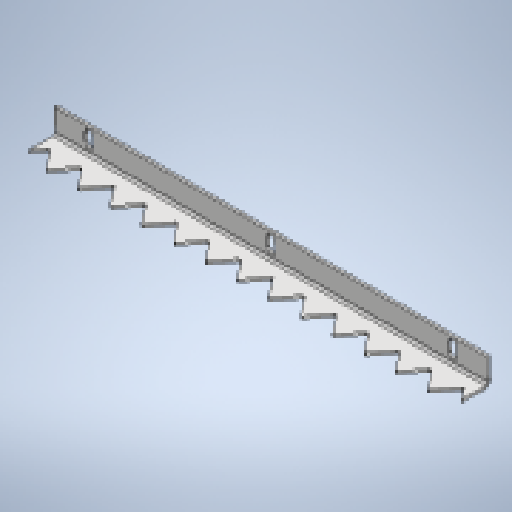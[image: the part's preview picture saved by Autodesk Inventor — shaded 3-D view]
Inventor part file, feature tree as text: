
AUTODESK INVENTOR PART (.ipt)
format: ipt  version: 2025.1 (Build 291241020, 241B)  size: 320,000 bytes
history: native  units: mm
features: other x5, sheet_metal_op x4, sketch x4, pattern_linear x2, projected_geometry x1
ambient origin geometry x8: Origin, YZ Plane, XZ Plane, XY Plane, X Axis, Y Axis, Z Axis, Center Point
bodies: Solid1 (feature_tree)
feature tree (16):
  sheet_metal_op  "Face1"
  pattern_linear  "Rectangular Pattern1"  Count1=4  [1 undecoded]
  sheet_metal_op  "Flange3"
  pattern_linear  "Rectangular Pattern2"  Count1=2  [1 undecoded]
  sketch  "Sketch1"  dims[d0=476.0mm d1=40.0mm]
  other  "Plate1"
  sketch  "Sketch6"  dims[d2=3.0mm d33=20.0mm]
  projected_geometry  "Projected Loop1"
  sketch  "Sketch7"  dims[d35=3.0mm]
  other  "Plate4"
  sheet_metal_op  "Bend3"
  sheet_metal_op  "Corner3"
  sketch  "Sketch8"  dims[d36=3.0mm d37=0.0mm d38=440.0mm d40=35.0mm d41=3.0mm d42=1.5mm d43=6.0mm d44=2.75mm d45=30.0mm d46=16.057029mm d47=2.75mm d48=12.0mm d49=3.0mm d50=2.75mm d51=9.0mm d53=10.0mm d54=3.0mm d55=0.0mm d56=30.0mm d58=200.0mm d79=7.0mm d81=0.5mm d82=75.0deg]
  other  "Cut1"
  other  "Cut2"
  other  "Definition1"
note: 2 required parameter values undecoded (feature->parameter linkage not recoverable at this tier; creation-order binding heuristic only, values carry confidence <= 0.55)
